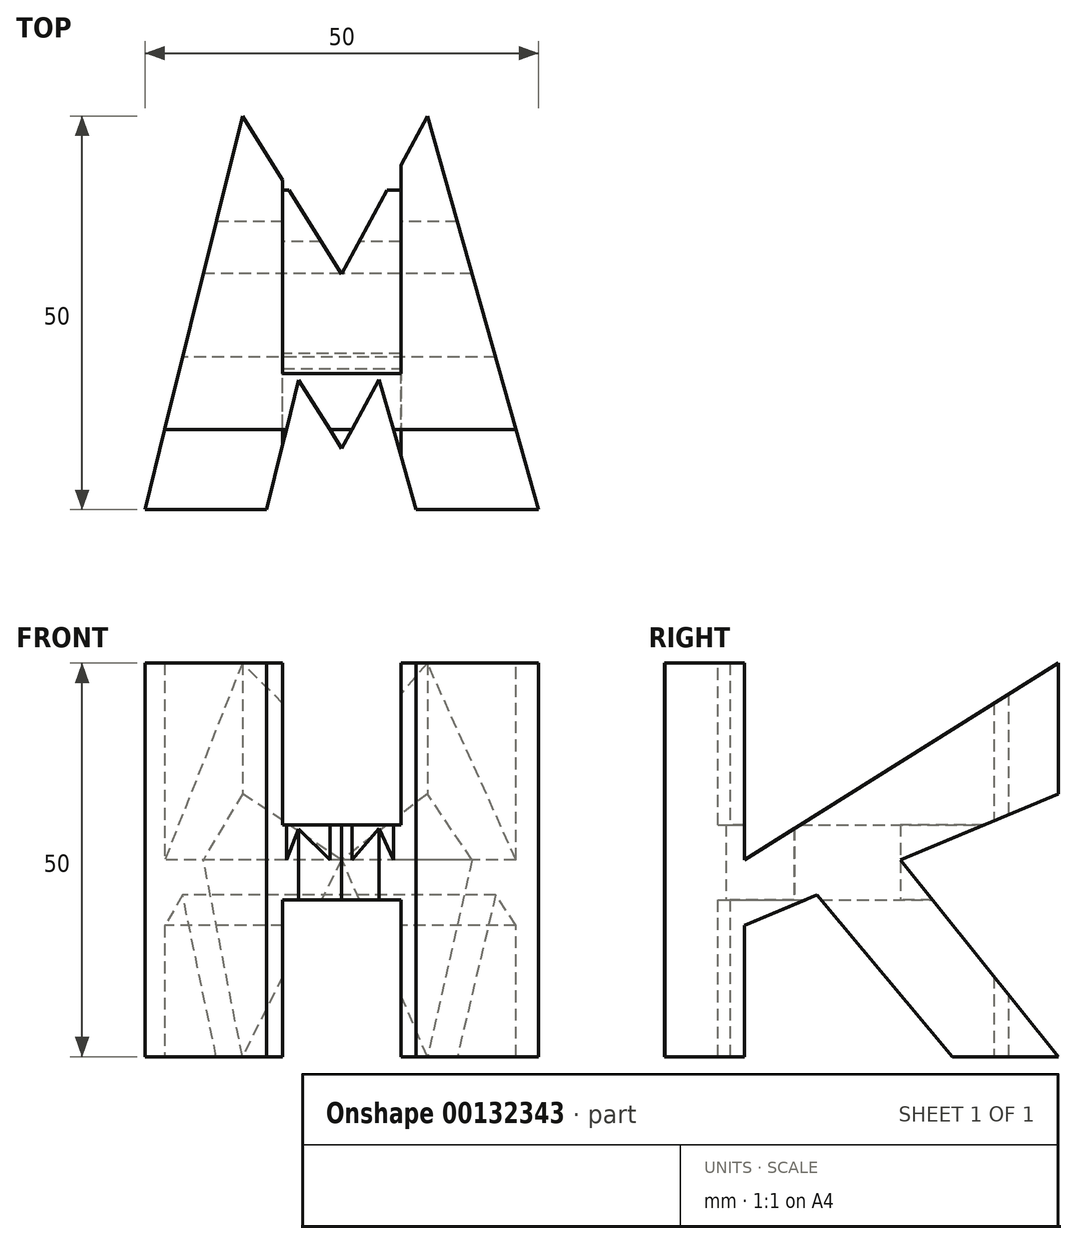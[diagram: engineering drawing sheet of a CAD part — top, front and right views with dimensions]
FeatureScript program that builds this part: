
annotation { "Feature Type Name" : "Feature", "Feature Type Description" : "" }
export const myFeature = defineFeature(function(context is Context, id is Id, definition is map)
    precondition{}
    {
        {
            var Q0;
            Q0=qCreatedBy(makeId("Front.planeOp"),FACE);
            var sketch = newSketch(context, id + "F0", { "sketchPlane" : qUnion([Q0])});
            skLineSegment(sketch, "E0.bottom", {"start": v(-25, 25) * mm, "end": v(-7.5, 25) * mm, "construction": true});
            skLineSegment(sketch, "E0.top", {"start": v(-25, -25) * mm, "end": v(-7.5, -25) * mm, "construction": true});
            skLineSegment(sketch, "E0.left", {"start": v(-25, 25) * mm, "end": v(-25, -25) * mm, "construction": true});
            skLineSegment(sketch, "E0.right", {"start": v(25, 25) * mm, "end": v(25, -25) * mm, "construction": true});
            skPoint(sketch, "E0.middle", {"position": v(0, 0) * mm});
            skLineSegment(sketch, "E1.top", {"start": v(-25, 25) * mm, "end": v(-7.5, 25) * mm});
            skLineSegment(sketch, "E1.left", {"start": v(-25, 10.4) * mm, "end": v(-25, 25) * mm});
            skLineSegment(sketch, "E1.right", {"start": v(25, 10.4) * mm, "end": v(25, 25) * mm});
            skLineSegment(sketch, "E2.top", {"start": v(-25, -25) * mm, "end": v(-7.5, -25) * mm});
            skLineSegment(sketch, "E2.left", {"start": v(-25, -13.94) * mm, "end": v(-25, -25) * mm});
            skLineSegment(sketch, "E2.right", {"start": v(25, -13.94) * mm, "end": v(25, -25) * mm});
            skLineSegment(sketch, "E3.bottom", {"start": v(-7.5, -25) * mm, "end": v(-25, -25) * mm});
            skLineSegment(sketch, "E3.top", {"start": v(-7.5, 25) * mm, "end": v(-25, 25) * mm});
            skLineSegment(sketch, "E3.left", {"start": v(-7.5, -25) * mm, "end": v(-7.5, -5.07) * mm});
            skLineSegment(sketch, "E3.right", {"start": v(-25, -25) * mm, "end": v(-25, 25) * mm});
            skLineSegment(sketch, "E4.bottom", {"start": v(-7.5, 4.45) * mm, "end": v(7.5, 4.45) * mm});
            skLineSegment(sketch, "E4.top", {"start": v(-7.5, -5.07) * mm, "end": v(7.5, -5.07) * mm});
            skLineSegment(sketch, "E5.bottom", {"start": v(7.5, 25) * mm, "end": v(25, 25) * mm});
            skLineSegment(sketch, "E5.top", {"start": v(7.5, -25) * mm, "end": v(25, -25) * mm});
            skLineSegment(sketch, "E5.left", {"start": v(7.5, 25) * mm, "end": v(7.5, 4.45) * mm});
            skLineSegment(sketch, "E5.right", {"start": v(25, 25) * mm, "end": v(25, -25) * mm});
            skLineSegment(sketch, "E6.trimOffspring", {"start": v(-7.5, 4.45) * mm, "end": v(-7.5, 25) * mm});
            skLineSegment(sketch, "E7.trimOffspring", {"start": v(7.5, -5.07) * mm, "end": v(7.5, -25) * mm});
            skLineSegment(sketch, "E8.trimOffspring", {"start": v(7.5, -25) * mm, "end": v(25, -25) * mm, "construction": true});
            skLineSegment(sketch, "E9.trimOffspring", {"start": v(7.5, 25) * mm, "end": v(25, 25) * mm, "construction": true});
            skSolve(sketch);
        }
        {
            var Q0;
            Q0=qCreatedBy(makeId("Top.planeOp"),FACE);
            var sketch = newSketch(context, id + "F1", { "sketchPlane" : qUnion([Q0])});
            skLineSegment(sketch, "E10.bottom", {"start": v(-25, 25) * mm, "end": v(25, 25) * mm, "construction": true});
            skLineSegment(sketch, "E10.top", {"start": v(-25, -25) * mm, "end": v(25, -25) * mm, "construction": true});
            skLineSegment(sketch, "E10.left", {"start": v(-25, 25) * mm, "end": v(-25, -25) * mm, "construction": true});
            skLineSegment(sketch, "E10.right", {"start": v(25, 25) * mm, "end": v(25, -25) * mm, "construction": true});
            skPoint(sketch, "E10.middle", {"position": v(0, 0) * mm});
            skLineSegment(sketch, "E11", {"start": v(-25, -25) * mm, "end": v(-12.63, 25) * mm});
            skLineSegment(sketch, "E12", {"start": v(-9.55, -25) * mm, "end": v(-5.48, -8.54) * mm});
            skLineSegment(sketch, "E13", {"start": v(-5.48, -8.54) * mm, "end": v(0, -17.23) * mm});
            skLineSegment(sketch, "E14", {"start": v(10.88, 25) * mm, "end": v(25, -24.96) * mm});
            skLineSegment(sketch, "E15", {"start": v(-12.63, 25) * mm, "end": v(0, 4.94) * mm});
            skLineSegment(sketch, "E16", {"start": v(0, 4.94) * mm, "end": v(10.88, 25) * mm});
            skLineSegment(sketch, "E17", {"start": v(4.75, -8.47) * mm, "end": v(0, -17.23) * mm});
            skLineSegment(sketch, "E18", {"start": v(4.75, -8.47) * mm, "end": v(9.42, -25) * mm});
            skLineSegment(sketch, "E19", {"start": v(-9.55, -25) * mm, "end": v(-25, -25) * mm});
            skLineSegment(sketch, "E20", {"start": v(9.42, -25) * mm, "end": v(25, -24.96) * mm});
            skSolve(sketch);
        }
        {
            var Q0;
            Q0=qCreatedBy(makeId("Right.planeOp"),FACE);
            var sketch = newSketch(context, id + "F2", { "sketchPlane" : qUnion([Q0])});
            skLineSegment(sketch, "E21.bottom", {"start": v(-25, 25) * mm, "end": v(25, 25) * mm, "construction": true});
            skLineSegment(sketch, "E21.top", {"start": v(-25, -25) * mm, "end": v(25, -25) * mm, "construction": true});
            skLineSegment(sketch, "E21.left", {"start": v(-25, 25) * mm, "end": v(-25, -25) * mm, "construction": true});
            skLineSegment(sketch, "E21.right", {"start": v(25, 25) * mm, "end": v(25, -25) * mm, "construction": true});
            skPoint(sketch, "E21.middle", {"position": v(0, 0) * mm});
            skLineSegment(sketch, "E22.bottom", {"start": v(-14.82, -25) * mm, "end": v(-25, -25) * mm});
            skLineSegment(sketch, "E22.top", {"start": v(-14.82, 25) * mm, "end": v(-25, 25) * mm});
            skLineSegment(sketch, "E22.left", {"start": v(-14.82, -25) * mm, "end": v(-14.82, -8.32) * mm});
            skLineSegment(sketch, "E22.right", {"start": v(-25, -25) * mm, "end": v(-25, 25) * mm});
            skLineSegment(sketch, "E23", {"start": v(-14.82, 0) * mm, "end": v(25, 25) * mm});
            skLineSegment(sketch, "E24", {"start": v(-14.82, -8.32) * mm, "end": v(-5.66, -4.47) * mm});
            skLineSegment(sketch, "E25", {"start": v(4.99, 0) * mm, "end": v(25, -25) * mm});
            skLineSegment(sketch, "E26", {"start": v(-5.66, -4.47) * mm, "end": v(11.6, -25) * mm});
            skLineSegment(sketch, "E27.trimOffspring", {"start": v(4.99, 0) * mm, "end": v(25, 8.4) * mm});
            skLineSegment(sketch, "E28.trimOffspring", {"start": v(-14.82, 0) * mm, "end": v(-14.82, 25) * mm});
            skLineSegment(sketch, "E29", {"start": v(25, 25) * mm, "end": v(25, 8.4) * mm});
            skLineSegment(sketch, "E30", {"start": v(25, -25) * mm, "end": v(8.05, -25) * mm});
            skSolve(sketch);
        }
        {
            var Q0;
            Q0 = qSketchRegion(id + "F0", true);
            extrude(context, id + "F3", {"entities" : qUnion([Q0]), "endBound" : BoundingType.SYMMETRIC, "depth" : 50 * mm});
        }
        {
            var Q0;
            Q0 = qSketchRegion(id + "F2", true);
            extrude(context, id + "F4", {"entities" : qUnion([Q0]), "operationType" : NewBodyOperationType.INTERSECT, "endBound" : BoundingType.SYMMETRIC, "depth" : 50 * mm});
        }
        {
            var Q0;
            Q0 = qSketchRegion(id + "F1", true);
            extrude(context, id + "F5", {"entities" : qUnion([Q0]), "operationType" : NewBodyOperationType.INTERSECT, "endBound" : BoundingType.SYMMETRIC, "depth" : 50 * mm});
        }
    });
